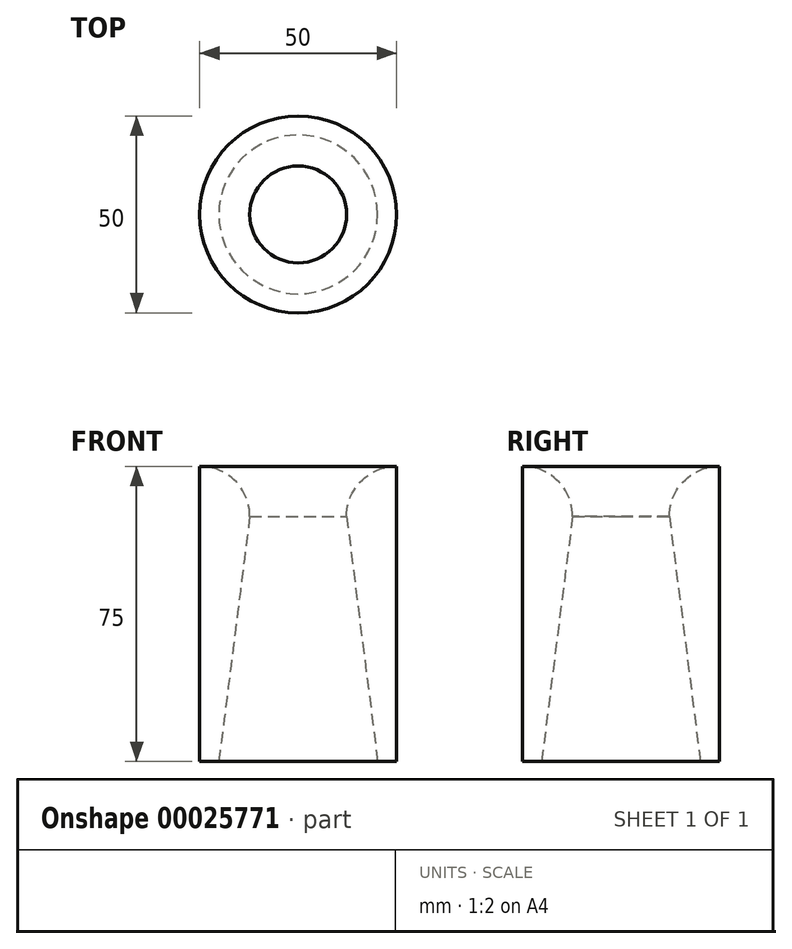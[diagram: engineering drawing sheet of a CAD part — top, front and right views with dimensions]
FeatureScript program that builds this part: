
annotation { "Feature Type Name" : "Feature", "Feature Type Description" : "" }
export const myFeature = defineFeature(function(context is Context, id is Id, definition is map)
    precondition{}
    {
        {
            var Q0;
            Q0=qCreatedBy(makeId("Front.planeOp"),FACE);
            var sketch = newSketch(context, id + "F0", { "sketchPlane" : qUnion([Q0])});
            skLineSegment(sketch, "E0", {"start": v(0, 0) * mm, "end": v(25, 0) * mm});
            skLineSegment(sketch, "E1", {"start": v(25, 0) * mm, "end": v(25, 75) * mm});
            skArc(sketch, "E2", {"start": v(25, 75) * mm, "mid": v(16.02, 71.28) * mm, "end": v(12.3, 62.3) * mm});
            skLineSegment(sketch, "E3", {"start": v(25, 62.3) * mm, "end": v(12.3, 62.3) * mm, "construction": true});
            skLineSegment(sketch, "E4", {"start": v(12.3, 62.3) * mm, "end": v(20.17, 0) * mm});
            skLineSegment(sketch, "E5", {"start": v(0, 0) * mm, "end": v(0, 76.07) * mm, "construction": true});
            skSolve(sketch);
        }
        {
            var Q0;
            Q0 = qSketchRegion(id + "F0", true);
            var Q1;
            Q1=sQuery(id+"F0.wireOp",EDGE,"E5");
            revolve(context, id + "F1", {"surfaceOperationType" : NewSurfaceOperationType.NEW, "entities" : qUnion([Q0]), "axis" : qUnion([Q1]), "revolveType" : RevolveType.FULL});
        }
    });
